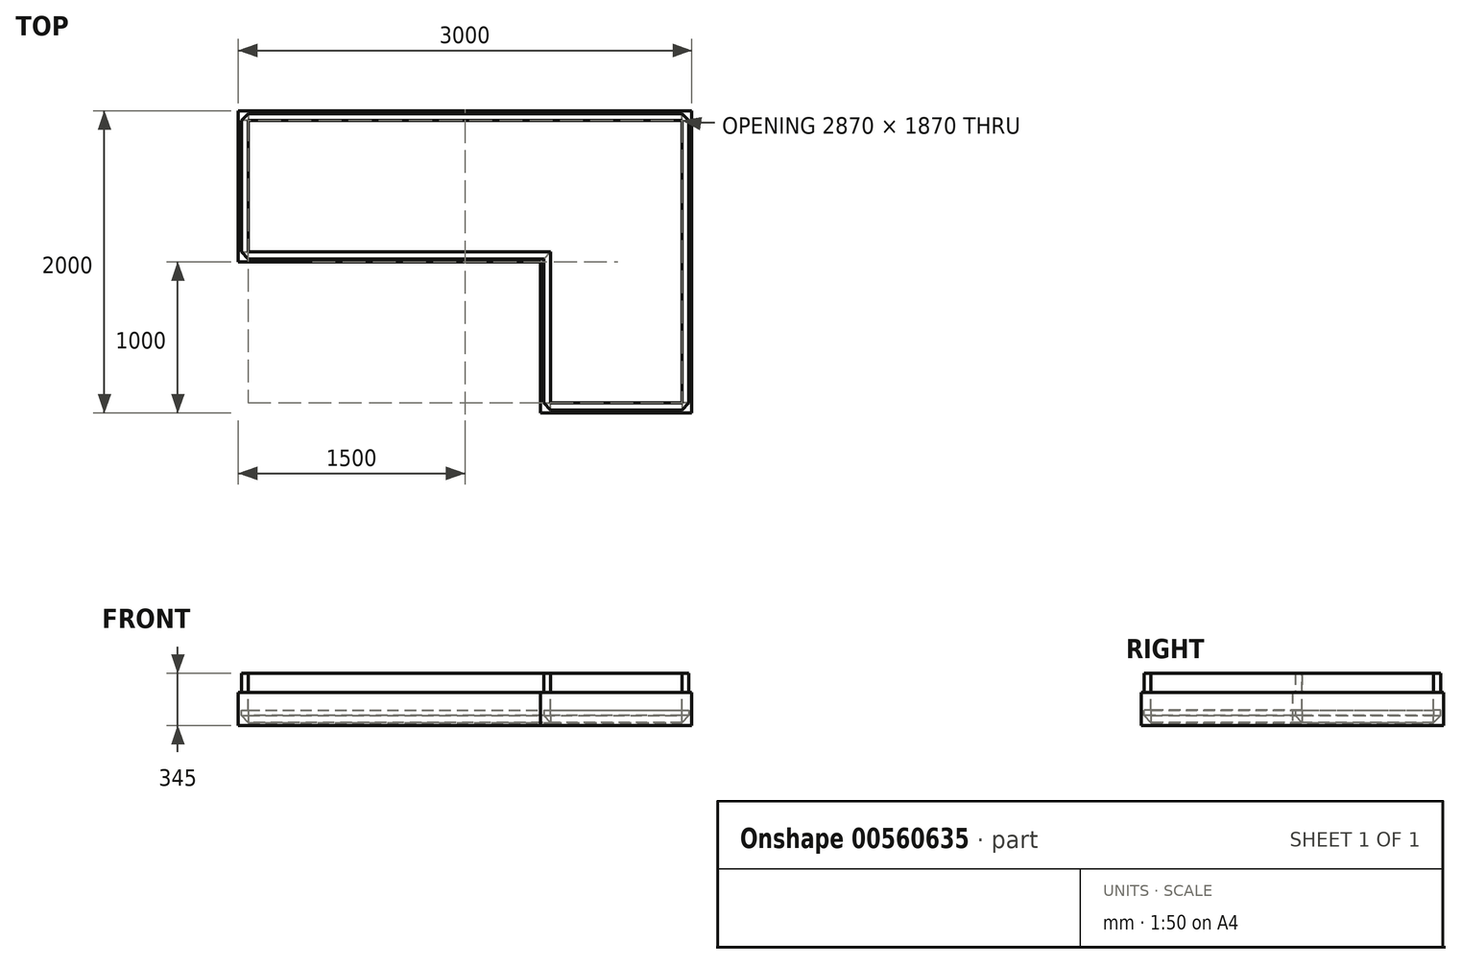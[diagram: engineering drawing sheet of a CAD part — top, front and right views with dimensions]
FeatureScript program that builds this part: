
annotation { "Feature Type Name" : "Feature", "Feature Type Description" : "" }
export const myFeature = defineFeature(function(context is Context, id is Id, definition is map)
    precondition{}
    {
        {
            var Q0;
            Q0=qCreatedBy(makeId("Top.planeOp"),FACE);
            var sketch = newSketch(context, id + "F0", { "sketchPlane" : qUnion([Q0])});
            skLineSegment(sketch, "E0.bottom", {"start": v(0, 0) * mm, "end": v(-3000, 0) * mm});
            skLineSegment(sketch, "E0.top", {"start": v(0, -1000) * mm, "end": v(-3000, -1000) * mm});
            skLineSegment(sketch, "E0.left", {"start": v(0, 0) * mm, "end": v(0, -1000) * mm});
            skLineSegment(sketch, "E0.right", {"start": v(-3000, 0) * mm, "end": v(-3000, -1000) * mm});
            skLineSegment(sketch, "E1.bottom", {"start": v(0, -1000) * mm, "end": v(-1000, -1000) * mm});
            skLineSegment(sketch, "E1.top", {"start": v(0, -2000) * mm, "end": v(-1000, -2000) * mm});
            skLineSegment(sketch, "E1.left", {"start": v(0, -1000) * mm, "end": v(0, -2000) * mm});
            skLineSegment(sketch, "E1.right", {"start": v(-1000, -1000) * mm, "end": v(-1000, -2000) * mm});
            skSolve(sketch);
        }
        {
            var Q0;
            Q0 = qSketchRegion(id + "F0", true);
            extrude(context, id + "F1", {"entities" : qUnion([Q0]), "depth" : 220 * mm, "offsetDistance" : 25 * mm});
        }
        {
            var Q0;
            Q0=makeQuery(id+"F1.opExtrude","CAP_FACE",FACE,{"disambiguationData":[OSD([sQuery(id+"F0.wireOp",EDGE,"E0.bottom"),sQuery(id+"F0.wireOp",EDGE,"E0.top"),sQuery(id+"F0.wireOp",EDGE,"E0.left"),sQuery(id+"F0.wireOp",EDGE,"E0.right"),sQuery(id+"F0.wireOp",EDGE,"E1.top"),sQuery(id+"F0.wireOp",EDGE,"E1.left"),sQuery(id+"F0.wireOp",EDGE,"E1.right")])],"isStart":false});
            shell(context, id + "F2", {"entities" : qUnion([Q0]), "thickness" : 20 * mm});
        }
        {
            var Q0;
            Q0=makeQuery(id+"F2.opShell","OFFSET_EDGE",EDGE,{"disambiguationData":[OSD([sQuery(id+"F0.wireOp",EDGE,"E0.bottom"),sQuery(id+"F0.wireOp",EDGE,"E0.right")])]});
            var Q1;
            {var subQ0=sQuery(id+"F0.wireOp",EDGE,"E0.bottom");Q1=makeQuery(id+"F2.opShell","OFFSET_EDGE",EDGE,{"disambiguationData":[OSD([subQ0]),TDD([makeQuery(id+"F1.opExtrude","CAP_EDGE",EDGE,{"disambiguationData":[OSD([subQ0])],"isStart":true})])]});}
            var Q2;
            {var subQ0=sQuery(id+"F0.wireOp",EDGE,"E0.right");Q2=makeQuery(id+"F2.opShell","OFFSET_EDGE",EDGE,{"disambiguationData":[OSD([subQ0]),TDD([makeQuery(id+"F1.opExtrude","CAP_EDGE",EDGE,{"disambiguationData":[OSD([subQ0])],"isStart":true})])]});}
            var Q3;
            Q3=makeQuery(id+"F2.opShell","OFFSET_EDGE",EDGE,{"disambiguationData":[OSD([sQuery(id+"F0.wireOp",EDGE,"E0.top"),sQuery(id+"F0.wireOp",EDGE,"E0.right")])]});
            var Q4;
            {var subQ0=sQuery(id+"F0.wireOp",EDGE,"E0.top");Q4=makeQuery(id+"F2.opShell","OFFSET_EDGE",EDGE,{"disambiguationData":[OSD([subQ0]),TDD([makeQuery(id+"F1.opExtrude","CAP_EDGE",EDGE,{"disambiguationData":[OSD([subQ0])],"isStart":true})])]});}
            var Q5;
            Q5=makeQuery(id+"F2.opShell","OFFSET_EDGE",EDGE,{"disambiguationData":[OSD([sQuery(id+"F0.wireOp",EDGE,"E0.bottom"),sQuery(id+"F0.wireOp",EDGE,"E0.left")])]});
            var Q6;
            {var subQ0=sQuery(id+"F0.wireOp",EDGE,"E1.left");var subQ1=sQuery(id+"F0.wireOp",EDGE,"E0.left");Q6=makeQuery(id+"F2.opShell","OFFSET_EDGE",EDGE,{"disambiguationData":[OSD([subQ1,subQ0]),TDD([makeQuery(id+"F1.opExtrude","CAP_EDGE",EDGE,{"disambiguationData":[OSD([subQ1,subQ0])],"isStart":true})])]});}
            var Q7;
            Q7=makeQuery(id+"F2.opShell","OFFSET_EDGE",EDGE,{"disambiguationData":[OSD([sQuery(id+"F0.wireOp",EDGE,"E1.top"),sQuery(id+"F0.wireOp",EDGE,"E1.right")])]});
            var Q8;
            {var subQ0=sQuery(id+"F0.wireOp",EDGE,"E1.right");Q8=makeQuery(id+"F2.opShell","OFFSET_EDGE",EDGE,{"disambiguationData":[OSD([subQ0]),TDD([makeQuery(id+"F1.opExtrude","CAP_EDGE",EDGE,{"disambiguationData":[OSD([subQ0])],"isStart":true})])]});}
            var Q9;
            {var subQ0=sQuery(id+"F0.wireOp",EDGE,"E1.top");Q9=makeQuery(id+"F2.opShell","OFFSET_EDGE",EDGE,{"disambiguationData":[OSD([subQ0]),TDD([makeQuery(id+"F1.opExtrude","CAP_EDGE",EDGE,{"disambiguationData":[OSD([subQ0])],"isStart":true})])]});}
            var Q10;
            Q10=makeQuery(id+"F2.opShell","OFFSET_EDGE",EDGE,{"disambiguationData":[OSD([sQuery(id+"F0.wireOp",EDGE,"E1.top"),sQuery(id+"F0.wireOp",EDGE,"E1.left")])]});
            chamfer(context, id + "F3", {"entities" : qUnion([Q0, Q1, Q2, Q3, Q4, Q5, Q6, Q7, Q8, Q9, Q10]), "width" : 45 * mm, "tangentPropagation" : true});
        }
        {
            var Q0;
            Q0=makeQuery(id+"F2.opShell","OFFSET_FACE",FACE,{"disambiguationData":[OSD([sQuery(id+"F0.wireOp",EDGE,"E0.bottom")])]});
            var sketch = newSketch(context, id + "F4", { "sketchPlane" : qUnion([Q0])});
            skLineSegment(sketch, "E2.bottom", {"start": v(-3280, 145) * mm, "end": v(-20, 145) * mm});
            skLineSegment(sketch, "E2.top", {"start": v(-3280, 100) * mm, "end": v(-20, 100) * mm});
            skLineSegment(sketch, "E2.left", {"start": v(-3280, 145) * mm, "end": v(-3280, 100) * mm});
            skLineSegment(sketch, "E2.right", {"start": v(-20, 145) * mm, "end": v(-20, 100) * mm});
            skSolve(sketch);
        }
        {
            var Q0;
            Q0 = qSketchRegion(id + "F4", true);
            extrude(context, id + "F5", {"entities" : qUnion([Q0]), "operationType" : NewBodyOperationType.ADD, "endBound" : BoundingType.UP_TO_NEXT, "depth" : 25 * mm, "offsetDistance" : 25 * mm});
        }
        {
            var Q0;
            Q0=makeQuery(id+"F5.opExtrude","SWEPT_FACE",FACE,{"disambiguationData":[OSD([sQuery(id+"F4.wireOp",EDGE,"E2.bottom")])]});
            var sketch = newSketch(context, id + "F6", { "sketchPlane" : qUnion([Q0])});
            skLineSegment(sketch, "E3", {"start": v(-2935, -65) * mm, "end": v(-2935, -935) * mm});
            skLineSegment(sketch, "E4", {"start": v(-2935, -935) * mm, "end": v(-935, -935) * mm});
            skLineSegment(sketch, "E5", {"start": v(-935, -935) * mm, "end": v(-935, -1935) * mm});
            skLineSegment(sketch, "E6", {"start": v(-935, -1935) * mm, "end": v(-65, -1935) * mm});
            skLineSegment(sketch, "E7", {"start": v(-65, -1935) * mm, "end": v(-65, -65) * mm});
            skLineSegment(sketch, "E8", {"start": v(-2935, -65) * mm, "end": v(-65, -65) * mm});
            skSolve(sketch);
        }
        {
            var Q0;
            Q0 = qSketchRegion(id + "F6", true);
            extrude(context, id + "F7", {"entities" : qUnion([Q0]), "operationType" : NewBodyOperationType.REMOVE, "oppositeDirection" : true, "depth" : 45 * mm, "offsetDistance" : 25 * mm});
        }
        {
            var Q0;
            Q0=makeQuery(id+"F5.opExtrude","SWEPT_FACE",FACE,{"disambiguationData":[OSD([sQuery(id+"F4.wireOp",EDGE,"E2.bottom")])]});
            var sketch = newSketch(context, id + "F8", { "sketchPlane" : qUnion([Q0])});
            skSolve(sketch);
        }
        {
            var Q0;
            Q0 = qSketchRegion(id + "F8", true);
            var Q1;
            {var subQ0=sQuery(id+"F4.wireOp",EDGE,"E2.bottom");Q1=makeQuery(id+"F8.imprint","IMPRINT",FACE,{"disambiguationData":[TD([[makeQuery(id+"F8.imprint","IMPRINT",EDGE,{"derivedFrom":makeQuery(id+"F5.opExtrude","CAP_EDGE",EDGE,{"disambiguationData":[OSD([subQ0])],"isStart":true})}),-1.0]])]});}
            var Q2;
            Q2=makeQuery(id+"F8.imprint","IMPRINT",FACE,{"disambiguationData":[TD([[makeQuery(id+"F8.imprint","IMPRINT",EDGE,{"derivedFrom":makeQuery(id+"F7.boolean.opBoolean","COPY",EDGE,{"derivedFrom":makeQuery(id+"F7.opExtrude","CAP_EDGE",EDGE,{"disambiguationData":[OSD([sQuery(id+"F6.wireOp",EDGE,"E3")])],"isStart":true})})}),1.0]])]});
            extrude(context, id + "F9", {"entities" : qUnion([Q0, Q1, Q2]), "operationType" : NewBodyOperationType.ADD, "depth" : 200 * mm, "offsetDistance" : 25 * mm});
        }
    });
